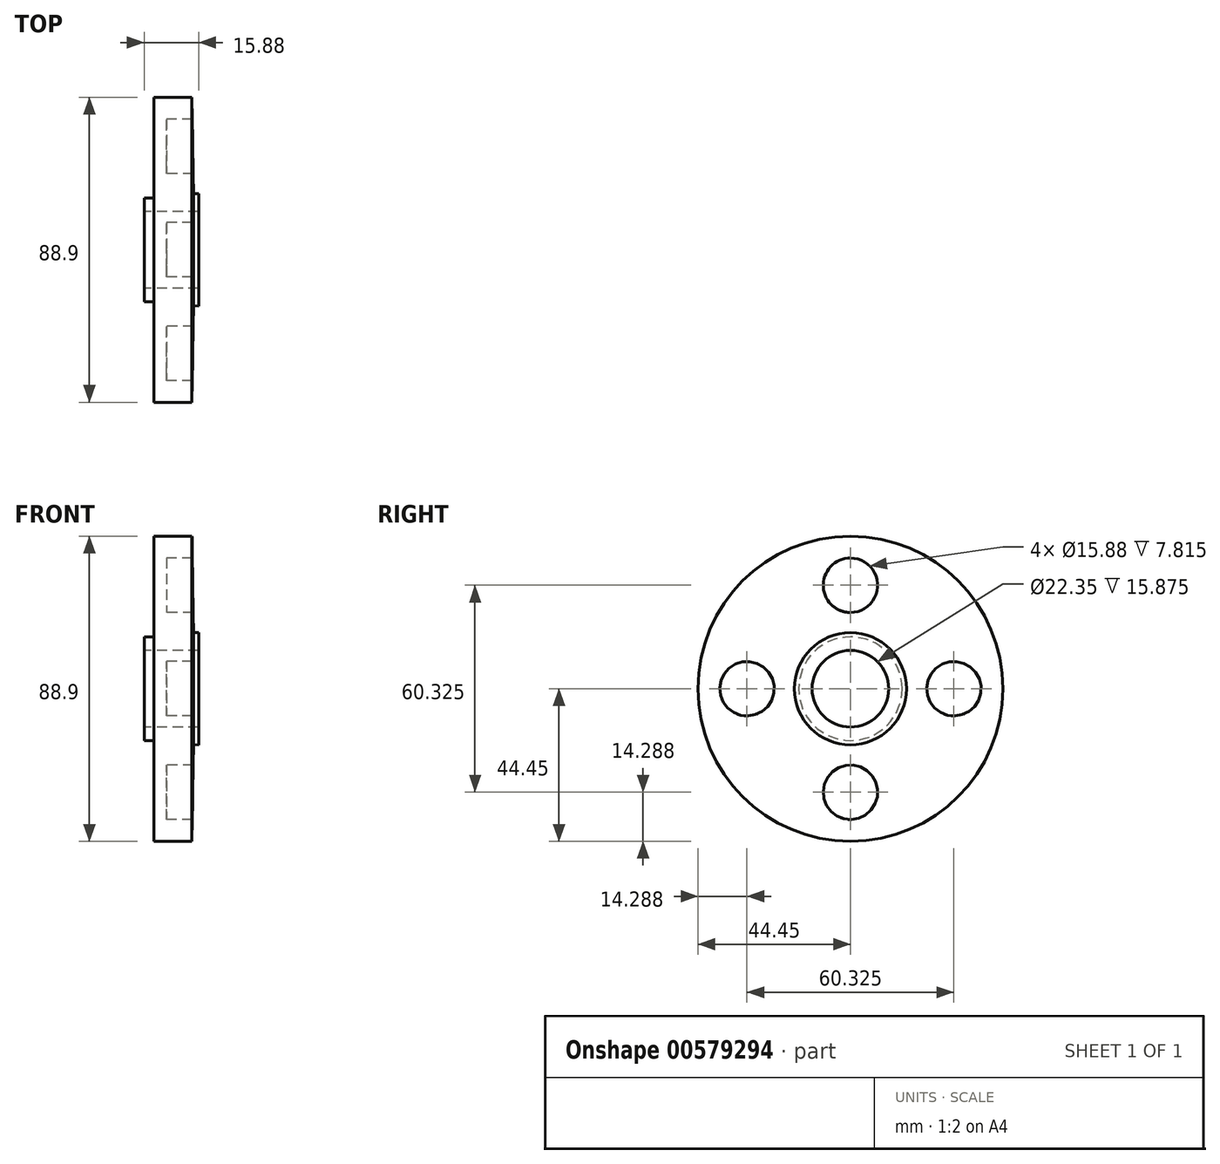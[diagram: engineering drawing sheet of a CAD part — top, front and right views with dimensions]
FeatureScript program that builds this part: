
annotation { "Feature Type Name" : "Feature", "Feature Type Description" : "" }
export const myFeature = defineFeature(function(context is Context, id is Id, definition is map)
    precondition{}
    {
        {
            var Q0;
            Q0=qCreatedBy(makeId("Front.planeOp"),FACE);
            var sketch = newSketch(context, id + "F0", { "sketchPlane" : qUnion([Q0])});
            skLineSegment(sketch, "E0", {"start": v(-24.64, 0) * mm, "end": v(25.17, 0) * mm, "construction": true});
            skLineSegment(sketch, "E1", {"start": v(-6.45, 11.18) * mm, "end": v(-6.45, 15.09) * mm});
            skLineSegment(sketch, "E2", {"start": v(-6.45, 15.09) * mm, "end": v(-3.62, 15.09) * mm});
            skLineSegment(sketch, "E3", {"start": v(-3.62, 15.09) * mm, "end": v(-3.62, 44.45) * mm});
            skLineSegment(sketch, "E4", {"start": v(-3.62, 44.45) * mm, "end": v(7.48, 44.45) * mm});
            skLineSegment(sketch, "E5", {"start": v(7.48, 44.45) * mm, "end": v(7.9, 16.32) * mm});
            skLineSegment(sketch, "E6", {"start": v(9.43, 11.18) * mm, "end": v(-6.45, 11.18) * mm});
            skLineSegment(sketch, "E7", {"start": v(7.9, 16.32) * mm, "end": v(9.43, 16.34) * mm});
            skLineSegment(sketch, "E8", {"start": v(9.43, 16.34) * mm, "end": v(9.43, 11.18) * mm});
            skSolve(sketch);
        }
        {
            var Q0;
            Q0 = qSketchRegion(id + "F0", true);
            var Q1;
            Q1=sQuery(id+"F0.wireOp",EDGE,"E0");
            revolve(context, id + "F1", {"entities" : qUnion([Q0]), "axis" : qUnion([Q1]), "revolveType" : RevolveType.FULL});
        }
        {
            var Q0;
            Q0=qCreatedBy(makeId("Right.planeOp"),FACE);
            var sketch = newSketch(context, id + "F2", { "sketchPlane" : qUnion([Q0])});
            skCircle(sketch, "E9", {"center": v(0, 0) * mm, "radius": 30.16 * mm, "construction": true});
            skCircle(sketch, "E10", {"center": v(0, 30.16) * mm, "radius": 7.94 * mm});
            skCircle(sketch, "E11.1.0", {"center": v(-30.16, 0) * mm, "radius": 7.94 * mm});
            skCircle(sketch, "E11.2.0", {"center": v(0, -30.16) * mm, "radius": 7.94 * mm});
            skCircle(sketch, "E11.3.0", {"center": v(30.16, 0) * mm, "radius": 7.94 * mm});
            skSolve(sketch);
        }
        {
            var Q0;
            Q0 = qSketchRegion(id + "F2", true);
            extrude(context, id + "F3", {"entities" : qUnion([Q0]), "operationType" : NewBodyOperationType.REMOVE, "endBound" : BoundingType.THROUGH_ALL, "depth" : 25.4 * mm, "offsetDistance" : 25.4 * mm});
        }
    });
